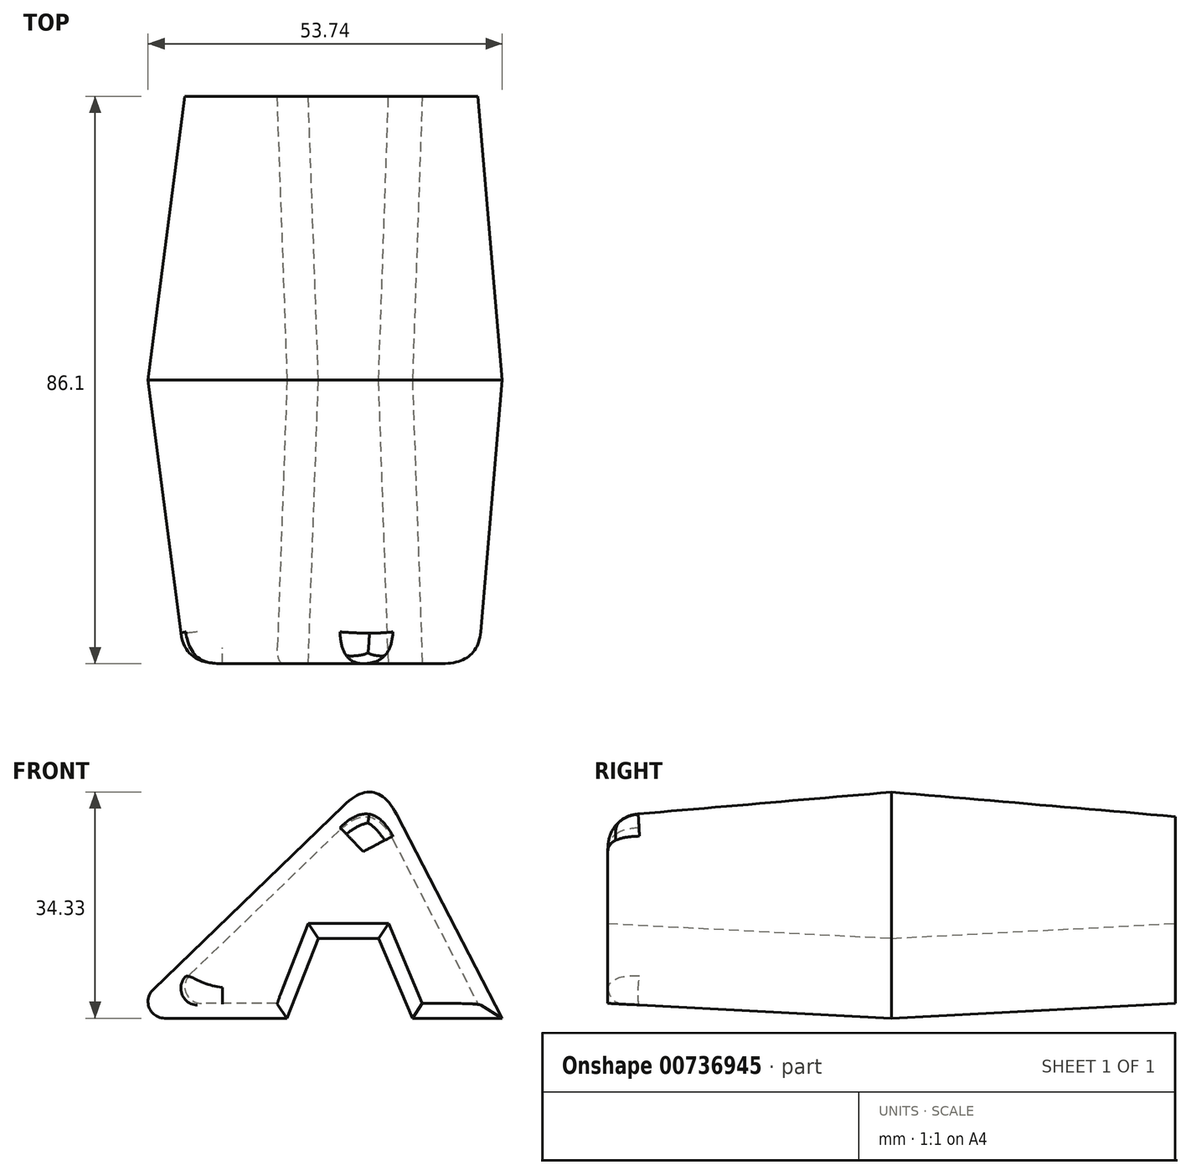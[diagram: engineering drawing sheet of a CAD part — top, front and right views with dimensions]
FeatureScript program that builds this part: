
annotation { "Feature Type Name" : "Feature", "Feature Type Description" : "" }
export const myFeature = defineFeature(function(context is Context, id is Id, definition is map)
    precondition{}
    {
        {
            var Q0;
            Q0=qCreatedBy(makeId("Front.planeOp"),FACE);
            var sketch = newSketch(context, id + "F0", { "sketchPlane" : qUnion([Q0])});
            skLineSegment(sketch, "E0", {"start": v(0, 0) * mm, "end": v(38.28, 36.98) * mm});
            skLineSegment(sketch, "E1", {"start": v(38.28, 36.98) * mm, "end": v(57.47, 0) * mm});
            skLineSegment(sketch, "E2", {"start": v(57.47, 0) * mm, "end": v(43.83, 0) * mm});
            skLineSegment(sketch, "E3", {"start": v(24.81, 0) * mm, "end": v(29.58, 12.13) * mm});
            skLineSegment(sketch, "E4", {"start": v(29.58, 12.13) * mm, "end": v(38.7, 12.13) * mm});
            skLineSegment(sketch, "E5", {"start": v(38.7, 12.13) * mm, "end": v(43.83, 0) * mm});
            skLineSegment(sketch, "E6.trimOffspring", {"start": v(24.81, 0) * mm, "end": v(0, 0) * mm});
            skSolve(sketch);
        }
        {
            var Q0;
            Q0=makeQuery(id+"F0.imprint","IMPRINT",FACE,{"disambiguationData":[TD([[makeQuery(id+"F0.imprint","IMPRINT",EDGE,{"derivedFrom":sQuery(id+"F0.wireOp",EDGE,"E0")}),-1.0]])]});
            extrude(context, id + "F1", {"entities" : qUnion([Q0]), "endBound" : BoundingType.SYMMETRIC, "depth" : 86.1 * mm, "offsetDistance" : 25.4 * mm, "hasDraft" : true, "draftAngle" : 3 * degree, "draftPullDirection" : true, "hasSecondDirection" : true, "secondDirectionOppositeDirection" : true, "secondDirectionDepth" : 25.4 * mm});
        }
        {
            var Q0;
            Q0=makeQuery(id+"F1.*.split.splitOp","SPLIT",EDGE,{"derivedFrom":makeQuery(id+"F1.opExtrude","SWEPT_EDGE",EDGE,{"disambiguationData":[OSD([sQuery(id+"F0.wireOp",EDGE,"E0"),sQuery(id+"F0.wireOp",EDGE,"E1")])]})});
            var Q1;
            Q1=makeQuery(id+"F1.*.split.splitOp","SPLIT",EDGE,{"derivedFrom":makeQuery(id+"F1.opExtrude","SWEPT_EDGE",EDGE,{"disambiguationData":[OSD([sQuery(id+"F0.wireOp",EDGE,"E0"),sQuery(id+"F0.wireOp",EDGE,"E1")])]}),"isFromBackBody":true});
            var Q2;
            Q2=makeQuery(id+"F1.opExtrude","CAP_EDGE",EDGE,{"disambiguationData":[OSD([sQuery(id+"F0.wireOp",EDGE,"E1")])],"isStart":false});
            var Q3;
            Q3=makeQuery(id+"F1.opExtrude","CAP_EDGE",EDGE,{"disambiguationData":[OSD([sQuery(id+"F0.wireOp",EDGE,"E0")])],"isStart":false});
            fillet(context, id + "F2", {"entities" : qUnion([Q0, Q1, Q2, Q3]), "radius" : 5.08 * mm, "tangentPropagation" : true, "rho" : 0.5, "crossSection" : FilletCrossSection.CONIC, "allowEdgeOverflow" : false});
        }
        {
            var Q0;
            Q0=makeQuery(id+"F1.*.split.splitOp","SPLIT",EDGE,{"derivedFrom":makeQuery(id+"F1.opExtrude","SWEPT_EDGE",EDGE,{"disambiguationData":[OSD([sQuery(id+"F0.wireOp",EDGE,"E0"),sQuery(id+"F0.wireOp",EDGE,"E6.trimOffspring")])]})});
            var Q1;
            Q1=makeQuery(id+"F1.*.split.splitOp","SPLIT",EDGE,{"derivedFrom":makeQuery(id+"F1.opExtrude","SWEPT_EDGE",EDGE,{"disambiguationData":[OSD([sQuery(id+"F0.wireOp",EDGE,"E0"),sQuery(id+"F0.wireOp",EDGE,"E6.trimOffspring")])]}),"isFromBackBody":true});
            fillet(context, id + "F3", {"entities" : qUnion([Q0, Q1]), "radius" : 2.54 * mm, "tangentPropagation" : true, "allowEdgeOverflow" : false});
        }
    });
